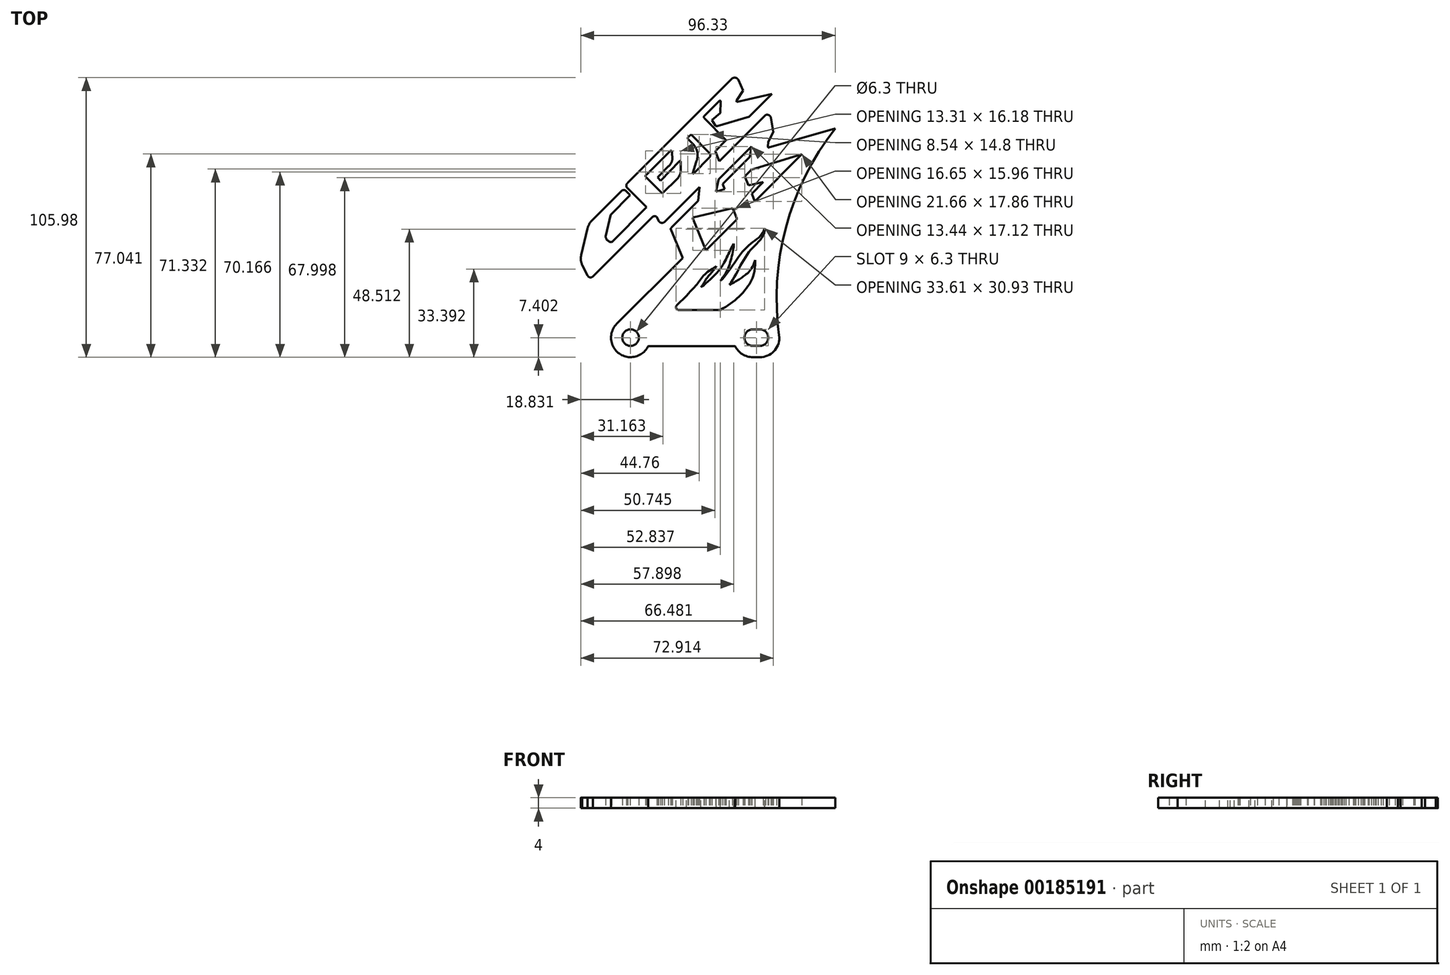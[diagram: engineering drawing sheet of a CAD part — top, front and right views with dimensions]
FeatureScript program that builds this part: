
annotation { "Feature Type Name" : "Feature", "Feature Type Description" : "" }
export const myFeature = defineFeature(function(context is Context, id is Id, definition is map)
    precondition{}
    {
        {
            var Q0;
            Q0=qCreatedBy(makeId("Top.planeOp"),FACE);
            var sketch = newSketch(context, id + "F0", { "sketchPlane" : qUnion([Q0])});
            skCircle(sketch, "E0", {"center": v(-2.3, 4.3) * mm, "radius": 3.15 * mm});
            skLineSegment(sketch, "E1", {"start": v(-2.3, 4.3) * mm, "end": v(46.7, 4.3) * mm, "construction": true});
            skArc(sketch, "E2", {"start": v(46.7, 7.44) * mm, "mid": v(49.85, 4.3) * mm, "end": v(46.7, 1.14) * mm});
            skArc(sketch, "E3", {"start": v(44, 7.44) * mm, "mid": v(40.85, 4.3) * mm, "end": v(44, 1.14) * mm});
            skLineSegment(sketch, "E4", {"start": v(44, 7.44) * mm, "end": v(46.7, 7.44) * mm});
            skLineSegment(sketch, "E5", {"start": v(44, 1.14) * mm, "end": v(46.7, 1.14) * mm});
            skLineSegment(sketch, "E6", {"start": v(-2.43, 58.35) * mm, "end": v(-9.88, 50.9) * mm});
            skLineSegment(sketch, "E7", {"start": v(-9.88, 50.9) * mm, "end": v(-11.8, 42.68) * mm});
            skArc(sketch, "E8", {"start": v(-11.8, 42.68) * mm, "mid": v(-11.02, 41.15) * mm, "end": v(-9.44, 40.5) * mm});
            skLineSegment(sketch, "E9", {"start": v(-9.44, 40.5) * mm, "end": v(3.78, 53.71) * mm});
            skLineSegment(sketch, "E10", {"start": v(3.78, 53.71) * mm, "end": v(-3.53, 61.02) * mm});
            skArc(sketch, "E11", {"start": v(-3.3, 63.02) * mm, "mid": v(-3.9, 62.07) * mm, "end": v(-3.53, 61.02) * mm});
            skLineSegment(sketch, "E12", {"start": v(-2.43, 58.35) * mm, "end": v(-4, 59.93) * mm});
            skArc(sketch, "E13", {"start": v(-4, 59.93) * mm, "mid": v(-4.86, 60.29) * mm, "end": v(-5.72, 59.93) * mm});
            skLineSegment(sketch, "E14", {"start": v(-5.72, 59.93) * mm, "end": v(-17.05, 48.6) * mm});
            skArc(sketch, "E15", {"start": v(-17.05, 48.6) * mm, "mid": v(-18.02, 47.29) * mm, "end": v(-18.55, 45.74) * mm});
            skLineSegment(sketch, "E16", {"start": v(-18.55, 45.74) * mm, "end": v(-20.96, 35.68) * mm});
            skArc(sketch, "E17", {"start": v(-20.96, 35.68) * mm, "mid": v(-21.1, 33.72) * mm, "end": v(-20.6, 31.82) * mm});
            skArc(sketch, "E18", {"start": v(-18.63, 27.88) * mm, "mid": v(-17.66, 27.15) * mm, "end": v(-16.5, 27.54) * mm});
            skLineSegment(sketch, "E19", {"start": v(-20.6, 31.82) * mm, "end": v(-18.63, 27.88) * mm});
            skLineSegment(sketch, "E20", {"start": v(-16.5, 27.54) * mm, "end": v(5.96, 50) * mm});
            skArc(sketch, "E21", {"start": v(7.72, 50) * mm, "mid": v(6.84, 50.36) * mm, "end": v(5.96, 50) * mm});
            skArc(sketch, "E22", {"start": v(8.3, 48.61) * mm, "mid": v(9.27, 47.85) * mm, "end": v(10.48, 48.1) * mm});
            skArc(sketch, "E23", {"start": v(3.78, 66.14) * mm, "mid": v(3.39, 65.69) * mm, "end": v(3.56, 65.12) * mm});
            skArc(sketch, "E24", {"start": v(15.51, 64.72) * mm, "mid": v(16.34, 65.93) * mm, "end": v(16.68, 67.35) * mm});
            skArc(sketch, "E25", {"start": v(12.07, 69.23) * mm, "mid": v(13, 70.36) * mm, "end": v(13.5, 71.74) * mm});
            skArc(sketch, "E26", {"start": v(22.54, 70.9) * mm, "mid": v(23.03, 74.47) * mm, "end": v(21.38, 77.69) * mm});
            skArc(sketch, "E27", {"start": v(27.55, 72.58) * mm, "mid": v(27.9, 73.47) * mm, "end": v(27.48, 74.34) * mm});
            skArc(sketch, "E28", {"start": v(19.47, 80.28) * mm, "mid": v(19.37, 79.85) * mm, "end": v(19.57, 79.45) * mm});
            skArc(sketch, "E29", {"start": v(21.83, 49.99) * mm, "mid": v(21.35, 49.7) * mm, "end": v(21.38, 49.15) * mm});
            skArc(sketch, "E30", {"start": v(37.62, 48.82) * mm, "mid": v(37.9, 49.17) * mm, "end": v(37.92, 49.62) * mm});
            skArc(sketch, "E31", {"start": v(37.92, 94.26) * mm, "mid": v(37.84, 93.98) * mm, "end": v(37.92, 93.7) * mm});
            skArc(sketch, "E32", {"start": v(50.84, 87.74) * mm, "mid": v(50.04, 88.68) * mm, "end": v(48.8, 88.65) * mm});
            skLineSegment(sketch, "E33", {"start": v(-3.3, 63.02) * mm, "end": v(36.31, 102.63) * mm});
            skLineSegment(sketch, "E34", {"start": v(40.34, 98.02) * mm, "end": v(37.92, 94.26) * mm});
            skLineSegment(sketch, "E35", {"start": v(37.92, 93.7) * mm, "end": v(51.25, 96.71) * mm});
            skLineSegment(sketch, "E36", {"start": v(3.78, 66.14) * mm, "end": v(12.67, 75.02) * mm});
            skArc(sketch, "E37", {"start": v(13.38, 74.85) * mm, "mid": v(13.07, 75.14) * mm, "end": v(12.67, 75.02) * mm});
            skLineSegment(sketch, "E38", {"start": v(13.38, 74.85) * mm, "end": v(13.5, 71.74) * mm});
            skLineSegment(sketch, "E39", {"start": v(12.07, 69.23) * mm, "end": v(7.89, 65.02) * mm});
            skLineSegment(sketch, "E40", {"start": v(7.89, 65.02) * mm, "end": v(9.12, 63.8) * mm});
            skLineSegment(sketch, "E41", {"start": v(9.12, 63.8) * mm, "end": v(16.24, 71.16) * mm});
            skArc(sketch, "E42", {"start": v(16.7, 71) * mm, "mid": v(16.52, 71.23) * mm, "end": v(16.24, 71.16) * mm});
            skLineSegment(sketch, "E43", {"start": v(16.7, 71) * mm, "end": v(16.68, 67.35) * mm});
            skLineSegment(sketch, "E44", {"start": v(15.51, 64.72) * mm, "end": v(9.76, 58.96) * mm});
            skLineSegment(sketch, "E45", {"start": v(9.76, 58.96) * mm, "end": v(3.56, 65.12) * mm});
            skLineSegment(sketch, "E46", {"start": v(21.38, 77.69) * mm, "end": v(19.57, 79.45) * mm});
            skLineSegment(sketch, "E47", {"start": v(19.47, 80.28) * mm, "end": v(20.61, 81.33) * mm});
            skLineSegment(sketch, "E48", {"start": v(20.61, 81.33) * mm, "end": v(27.48, 74.34) * mm});
            skLineSegment(sketch, "E49", {"start": v(27.55, 72.58) * mm, "end": v(21.66, 66.6) * mm});
            skArc(sketch, "E50", {"start": v(21.29, 66.73) * mm, "mid": v(21.43, 66.54) * mm, "end": v(21.66, 66.6) * mm});
            skLineSegment(sketch, "E51", {"start": v(21.29, 66.73) * mm, "end": v(22.54, 70.9) * mm});
            skArc(sketch, "E52", {"start": v(38.53, 102.06) * mm, "mid": v(37.54, 102.82) * mm, "end": v(36.31, 102.63) * mm});
            skLineSegment(sketch, "E53", {"start": v(38.53, 102.06) * mm, "end": v(40.34, 98.02) * mm});
            skLineSegment(sketch, "E54", {"start": v(51.25, 96.71) * mm, "end": v(42.61, 88.07) * mm});
            skLineSegment(sketch, "E55", {"start": v(42.61, 88.07) * mm, "end": v(30.54, 84.52) * mm});
            skArc(sketch, "E56", {"start": v(29.77, 84.8) * mm, "mid": v(30.1, 84.53) * mm, "end": v(30.54, 84.52) * mm});
            skLineSegment(sketch, "E57", {"start": v(29.77, 84.8) * mm, "end": v(28.55, 86.74) * mm});
            skLineSegment(sketch, "E58", {"start": v(28.55, 86.74) * mm, "end": v(31.67, 89.51) * mm});
            skLineSegment(sketch, "E59", {"start": v(31.67, 89.51) * mm, "end": v(31.8, 93.84) * mm});
            skArc(sketch, "E60", {"start": v(31.8, 93.84) * mm, "mid": v(31.7, 94.07) * mm, "end": v(31.44, 94.13) * mm});
            skLineSegment(sketch, "E61", {"start": v(31.44, 94.13) * mm, "end": v(25.73, 88.48) * mm});
            skLineSegment(sketch, "E62", {"start": v(25.56, 87.6) * mm, "end": v(33.88, 79.13) * mm});
            skArc(sketch, "E63", {"start": v(25.73, 88.48) * mm, "mid": v(25.5, 88.07) * mm, "end": v(25.56, 87.6) * mm});
            skLineSegment(sketch, "E64", {"start": v(33.88, 79.13) * mm, "end": v(29.94, 75.08) * mm});
            skArc(sketch, "E65", {"start": v(29.94, 75.08) * mm, "mid": v(29.9, 74.92) * mm, "end": v(29.94, 74.76) * mm});
            skLineSegment(sketch, "E66", {"start": v(29.94, 74.76) * mm, "end": v(31.37, 71.23) * mm});
            skLineSegment(sketch, "E67", {"start": v(31.37, 71.23) * mm, "end": v(48.8, 88.65) * mm});
            skLineSegment(sketch, "E68", {"start": v(50.84, 87.74) * mm, "end": v(51.82, 82.18) * mm});
            skLineSegment(sketch, "E69", {"start": v(51.82, 82.18) * mm, "end": v(49.9, 78.5) * mm});
            skLineSegment(sketch, "E70", {"start": v(49.9, 78.5) * mm, "end": v(49.72, 76.8) * mm});
            skArc(sketch, "E71", {"start": v(49.72, 76.8) * mm, "mid": v(49.78, 76.53) * mm, "end": v(50, 76.37) * mm});
            skLineSegment(sketch, "E72", {"start": v(50, 76.37) * mm, "end": v(75.2, 83.58) * mm});
            skArc(sketch, "E73", {"start": v(75.2, 83.58) * mm, "mid": v(56.54, 46.1) * mm, "end": v(54.1, 4.3) * mm});
            skLineSegment(sketch, "E74", {"start": v(7.72, 50) * mm, "end": v(8.3, 48.61) * mm});
            skLineSegment(sketch, "E75", {"start": v(10.48, 48.1) * mm, "end": v(23.83, 61.45) * mm});
            skLineSegment(sketch, "E76", {"start": v(23.83, 61.45) * mm, "end": v(23.27, 56.13) * mm});
            skLineSegment(sketch, "E77", {"start": v(23.27, 56.13) * mm, "end": v(13.34, 46.2) * mm});
            skArc(sketch, "E78", {"start": v(13.34, 46.2) * mm, "mid": v(13.09, 45.88) * mm, "end": v(12.92, 45.51) * mm});
            skLineSegment(sketch, "E79", {"start": v(12.92, 45.51) * mm, "end": v(17.46, 34.51) * mm});
            skLineSegment(sketch, "E80", {"start": v(31.05, 64.35) * mm, "end": v(43.49, 76.78) * mm});
            skLineSegment(sketch, "E81", {"start": v(43.49, 76.78) * mm, "end": v(42.8, 72.78) * mm});
            skLineSegment(sketch, "E82", {"start": v(42.8, 72.78) * mm, "end": v(32.58, 62.55) * mm});
            skLineSegment(sketch, "E83", {"start": v(32.58, 62.55) * mm, "end": v(33.33, 60.57) * mm});
            skLineSegment(sketch, "E84", {"start": v(33.33, 60.57) * mm, "end": v(30.05, 59.66) * mm});
            skLineSegment(sketch, "E85", {"start": v(30.05, 59.66) * mm, "end": v(31.05, 64.35) * mm});
            skLineSegment(sketch, "E86", {"start": v(40.95, 65.47) * mm, "end": v(43.49, 68) * mm});
            skLineSegment(sketch, "E87", {"start": v(43.49, 68) * mm, "end": v(62.61, 73.82) * mm});
            skLineSegment(sketch, "E88", {"start": v(62.61, 73.82) * mm, "end": v(44.76, 55.96) * mm});
            skLineSegment(sketch, "E89", {"start": v(44.76, 55.96) * mm, "end": v(43.58, 58.81) * mm});
            skLineSegment(sketch, "E90", {"start": v(43.58, 58.81) * mm, "end": v(48, 63.24) * mm});
            skLineSegment(sketch, "E91", {"start": v(48, 63.24) * mm, "end": v(42.35, 62.09) * mm});
            skLineSegment(sketch, "E92", {"start": v(42.35, 62.09) * mm, "end": v(40.95, 65.47) * mm});
            skLineSegment(sketch, "E93", {"start": v(21.83, 49.99) * mm, "end": v(36.37, 53.38) * mm});
            skLineSegment(sketch, "E94", {"start": v(36.37, 53.38) * mm, "end": v(37.92, 49.62) * mm});
            skLineSegment(sketch, "E95", {"start": v(37.62, 48.82) * mm, "end": v(26.22, 37.42) * mm});
            skLineSegment(sketch, "E96", {"start": v(26.22, 37.42) * mm, "end": v(21.38, 49.15) * mm});
            skLineSegment(sketch, "E97", {"start": v(4.38, 1.12) * mm, "end": v(37.32, 1.12) * mm});
            skLineSegment(sketch, "E98", {"start": v(17.46, 34.51) * mm, "end": v(-7.53, 9.52) * mm});
            skLineSegment(sketch, "E99", {"start": v(-135.63, 30.3) * mm, "end": v(-76.62, 89.3) * mm, "construction": true});
            skLineSegment(sketch, "E100", {"start": v(-135.63, 30.3) * mm, "end": v(-69.05, 30.3) * mm, "construction": true});
            skArc(sketch, "E101", {"start": v(-7.53, 9.52) * mm, "mid": v(-6.57, -1.75) * mm, "end": v(4.38, 1.12) * mm});
            skPoint(sketch, "E102.startSnap0", {"position": v(49.85, 4.3) * mm});
            skArc(sketch, "E103", {"start": v(54.1, 4.3) * mm, "mid": v(51.93, -0.94) * mm, "end": v(46.7, -3.1) * mm});
            skArc(sketch, "E104", {"start": v(44, -3.1) * mm, "mid": v(40.05, -1.96) * mm, "end": v(37.32, 1.12) * mm});
            skLineSegment(sketch, "E105", {"start": v(44, -3.1) * mm, "end": v(46.7, -3.1) * mm});
            skLineSegment(sketch, "E106", {"start": v(44, 1.14) * mm, "end": v(-11.73, 1.14) * mm, "construction": true});
            skLineSegment(sketch, "E107", {"start": v(26.22, 37.42) * mm, "end": v(65.96, 77.16) * mm, "construction": true});
            skSolve(sketch);
        }
        {
            var Q0;
            Q0 = qSketchRegion(id + "F0", true);
            extrude(context, id + "F1", {"entities" : qUnion([Q0]), "flatOperationType" : FlatOperationType.REMOVE, "offsetDistance" : 25 * mm, "depth" : 4 * mm, "domain" : OperationDomain.MODEL});
        }
        {
            var Q0;
            Q0=makeQuery(id+"F1.opExtrude","CAP_FACE",FACE,{"disambiguationData":[OSD([sQuery(id+"F0.wireOp",EDGE,"E0"),sQuery(id+"F0.wireOp",EDGE,"E2"),sQuery(id+"F0.wireOp",EDGE,"E3"),sQuery(id+"F0.wireOp",EDGE,"E4"),sQuery(id+"F0.wireOp",EDGE,"E5"),sQuery(id+"F0.wireOp",EDGE,"E6"),sQuery(id+"F0.wireOp",EDGE,"E7"),sQuery(id+"F0.wireOp",EDGE,"E8"),sQuery(id+"F0.wireOp",EDGE,"E9"),sQuery(id+"F0.wireOp",EDGE,"E10"),sQuery(id+"F0.wireOp",EDGE,"E11"),sQuery(id+"F0.wireOp",EDGE,"E12"),sQuery(id+"F0.wireOp",EDGE,"E13"),sQuery(id+"F0.wireOp",EDGE,"E14"),sQuery(id+"F0.wireOp",EDGE,"E15"),sQuery(id+"F0.wireOp",EDGE,"E16"),sQuery(id+"F0.wireOp",EDGE,"E17"),sQuery(id+"F0.wireOp",EDGE,"E18"),sQuery(id+"F0.wireOp",EDGE,"E19"),sQuery(id+"F0.wireOp",EDGE,"E20"),sQuery(id+"F0.wireOp",EDGE,"E21"),sQuery(id+"F0.wireOp",EDGE,"E22"),sQuery(id+"F0.wireOp",EDGE,"E23"),sQuery(id+"F0.wireOp",EDGE,"E24"),sQuery(id+"F0.wireOp",EDGE,"E25"),sQuery(id+"F0.wireOp",EDGE,"E26"),sQuery(id+"F0.wireOp",EDGE,"E27"),sQuery(id+"F0.wireOp",EDGE,"E28"),sQuery(id+"F0.wireOp",EDGE,"E29"),sQuery(id+"F0.wireOp",EDGE,"E30"),sQuery(id+"F0.wireOp",EDGE,"E31"),sQuery(id+"F0.wireOp",EDGE,"E32"),sQuery(id+"F0.wireOp",EDGE,"E33"),sQuery(id+"F0.wireOp",EDGE,"E34"),sQuery(id+"F0.wireOp",EDGE,"E35"),sQuery(id+"F0.wireOp",EDGE,"E36"),sQuery(id+"F0.wireOp",EDGE,"E37"),sQuery(id+"F0.wireOp",EDGE,"E38"),sQuery(id+"F0.wireOp",EDGE,"E39"),sQuery(id+"F0.wireOp",EDGE,"E40"),sQuery(id+"F0.wireOp",EDGE,"E41"),sQuery(id+"F0.wireOp",EDGE,"E42"),sQuery(id+"F0.wireOp",EDGE,"E43"),sQuery(id+"F0.wireOp",EDGE,"E44"),sQuery(id+"F0.wireOp",EDGE,"E45"),sQuery(id+"F0.wireOp",EDGE,"E46"),sQuery(id+"F0.wireOp",EDGE,"E47"),sQuery(id+"F0.wireOp",EDGE,"E48"),sQuery(id+"F0.wireOp",EDGE,"E49"),sQuery(id+"F0.wireOp",EDGE,"E50"),sQuery(id+"F0.wireOp",EDGE,"E51"),sQuery(id+"F0.wireOp",EDGE,"E52"),sQuery(id+"F0.wireOp",EDGE,"E53"),sQuery(id+"F0.wireOp",EDGE,"E54"),sQuery(id+"F0.wireOp",EDGE,"E55"),sQuery(id+"F0.wireOp",EDGE,"E56"),sQuery(id+"F0.wireOp",EDGE,"E57"),sQuery(id+"F0.wireOp",EDGE,"E58"),sQuery(id+"F0.wireOp",EDGE,"E59"),sQuery(id+"F0.wireOp",EDGE,"E60"),sQuery(id+"F0.wireOp",EDGE,"E61"),sQuery(id+"F0.wireOp",EDGE,"E62"),sQuery(id+"F0.wireOp",EDGE,"E63"),sQuery(id+"F0.wireOp",EDGE,"E64"),sQuery(id+"F0.wireOp",EDGE,"E65"),sQuery(id+"F0.wireOp",EDGE,"E66"),sQuery(id+"F0.wireOp",EDGE,"E67"),sQuery(id+"F0.wireOp",EDGE,"E68"),sQuery(id+"F0.wireOp",EDGE,"E69"),sQuery(id+"F0.wireOp",EDGE,"E70"),sQuery(id+"F0.wireOp",EDGE,"E71"),sQuery(id+"F0.wireOp",EDGE,"E72"),sQuery(id+"F0.wireOp",EDGE,"E73"),sQuery(id+"F0.wireOp",EDGE,"E74"),sQuery(id+"F0.wireOp",EDGE,"E75"),sQuery(id+"F0.wireOp",EDGE,"E76"),sQuery(id+"F0.wireOp",EDGE,"E77"),sQuery(id+"F0.wireOp",EDGE,"E78"),sQuery(id+"F0.wireOp",EDGE,"E79"),sQuery(id+"F0.wireOp",EDGE,"E80"),sQuery(id+"F0.wireOp",EDGE,"E81"),sQuery(id+"F0.wireOp",EDGE,"E82"),sQuery(id+"F0.wireOp",EDGE,"E83"),sQuery(id+"F0.wireOp",EDGE,"E84"),sQuery(id+"F0.wireOp",EDGE,"E85"),sQuery(id+"F0.wireOp",EDGE,"E86"),sQuery(id+"F0.wireOp",EDGE,"E87"),sQuery(id+"F0.wireOp",EDGE,"E88"),sQuery(id+"F0.wireOp",EDGE,"E89"),sQuery(id+"F0.wireOp",EDGE,"E90"),sQuery(id+"F0.wireOp",EDGE,"E91"),sQuery(id+"F0.wireOp",EDGE,"E92"),sQuery(id+"F0.wireOp",EDGE,"E93"),sQuery(id+"F0.wireOp",EDGE,"E94"),sQuery(id+"F0.wireOp",EDGE,"E95"),sQuery(id+"F0.wireOp",EDGE,"E96"),sQuery(id+"F0.wireOp",EDGE,"E97"),sQuery(id+"F0.wireOp",EDGE,"E98"),sQuery(id+"F0.wireOp",EDGE,"E101"),sQuery(id+"F0.wireOp",EDGE,"E103"),sQuery(id+"F0.wireOp",EDGE,"E104"),sQuery(id+"F0.wireOp",EDGE,"E105")])],"isStart":false});
            var sketch = newSketch(context, id + "F2", { "sketchPlane" : qUnion([Q0])});
            skFitSpline(sketch, "E108", {"points": [v(18.83, 20.17) * mm, v(23.4, 25.23) * mm, v(26.1, 28.58) * mm, v(30.2, 31.37) * mm], "startDerivative": vector(18.13, 20.1) * mm, "endDerivative": vector(7.4, 5.32) * mm});
            skFitSpline(sketch, "E109", {"points": [v(30.2, 31.37) * mm, v(26.52, 26.74) * mm, v(24.33, 23.38) * mm], "startDerivative": vector(-4.24, -6.76) * mm, "endDerivative": vector(-4.53, -5.3) * mm});
            skFitSpline(sketch, "E110", {"points": [v(24.33, 23.38) * mm, v(30.76, 29.3) * mm, v(34.1, 34.58) * mm, v(36.76, 39.98) * mm], "startDerivative": vector(9.39, 6.56) * mm, "endDerivative": vector(12.37, 24.56) * mm});
            skFitSpline(sketch, "E111", {"points": [v(36.76, 39.98) * mm, v(34.82, 31.01) * mm, v(31.75, 25.77) * mm], "startDerivative": vector(0.3, -11.86) * mm, "endDerivative": vector(-9.97, -14.65) * mm});
            skFitSpline(sketch, "E112", {"points": [v(31.75, 25.77) * mm, v(41.57, 38.45) * mm, v(48.51, 45.75) * mm], "startDerivative": vector(17.2, 15.82) * mm, "endDerivative": vector(10.1, 26.9) * mm});
            skFitSpline(sketch, "E113", {"points": [v(48.51, 45.75) * mm, v(42.94, 37.3) * mm, v(35.13, 24.29) * mm], "startDerivative": vector(2.13, -22.85) * mm, "endDerivative": vector(-16.23, -21.83) * mm});
            skFitSpline(sketch, "E114", {"points": [v(35.13, 24.29) * mm, v(40.25, 27.36) * mm, v(44.92, 33.65) * mm], "startDerivative": vector(15.48, 8.02) * mm, "endDerivative": vector(8.08, 22.28) * mm});
            skFitSpline(sketch, "E115", {"points": [v(31.67, 14.82) * mm, v(38.86, 19.91) * mm, v(43.26, 25.57) * mm, v(44.92, 33.65) * mm], "startDerivative": vector(24.35, 12.7) * mm, "endDerivative": vector(1.1, 40.8) * mm});
            skLineSegment(sketch, "E116.0", {"start": v(31.75, 25.77) * mm, "end": v(48.51, 45.75) * mm, "construction": true});
            skLineSegment(sketch, "E117.0", {"start": v(18.83, 20.17) * mm, "end": v(23.4, 25.23) * mm, "construction": true});
            skLineSegment(sketch, "E118", {"start": v(18.83, 20.17) * mm, "end": v(15.19, 16.52) * mm});
            skPoint(sketch, "E119.visualSharp", {"position": v(13.21, 14.55) * mm});
            skArc(sketch, "E119.filletArc", {"start": v(15.19, 16.52) * mm, "mid": v(14.97, 15.43) * mm, "end": v(15.9, 14.82) * mm});
            skLineSegment(sketch, "E120", {"start": v(31.67, 14.82) * mm, "end": v(15.9, 14.82) * mm});
            skSolve(sketch);
        }
        {
            var Q0;
            Q0 = qSketchRegion(id + "F2", true);
            extrude(context, id + "F3", {"entities" : qUnion([Q0]), "operationType" : NewBodyOperationType.REMOVE, "endBound" : BoundingType.THROUGH_ALL, "oppositeDirection" : true, "depth" : 25 * mm});
        }
    });
